# Revit family: C_BTCALU200_3D_CAD_MULT_Prod
name_source: partatom
category: Structural Connections
revit_build: Autodesk Revit 2015 (Build: 20140606_1530(x64)
units: mm (PartAtom-declared; Revit-internal decimal feet)

## types (1)
- C_BTCALU200_3D_CAD_MULT_Prod
    Default Elevation = 0 mm  [stored 0 ft]
    Density = 0.61 kg
    Description = Concealed beam hanger
    EPD = https://www.strongtie.eu
    ETA / DoP = https://www.strongtie.eu
    H = 200 mm  [stored 0.656168 ft]
    Manufacturer = Simpson Strong-Tie
    Model = BTCALU200
    Model Disclaimer = Contact Simpson Strong-Tie Company  for more information
    Model ID = 0080881108095439461087438277445270966215
    Name = BTCALU200
    ObjectType = BTCALU200
    Product Material = Aluminium
    Product Type = Concealed beam hanger
    Reference = BTCALU200
    SDD113 = SDD7.5x113
    SDD133 = SDD7.5x133
    SDD153 = SDD7.5x153
    SDD173 = SDD7.5x173
    SDD93 = SDD7.5x93
    STD10_100 = STD10X100
    STD10_120 = STD10X120
    STD10_140 = STD10X140
    STD10_160 = STD10X160
    STD10_60 = STD10X60
    STD10_80 = STD10X80
    STD12_100 = STD12X100
    STD12_120 = STD12X120
    STD12_140 = STD12X140
    STD12_160 = STD12X160
    STD12_60 = STD12X60
    STD12_80 = STD12X80
    STD8_100 = STD8X100
    STD8_120 = STD8X120
    STD8_140 = STD8X140
    STD8_160 = STD8X160
    STD8_60 = STD8X60
    STD8_80 = STD8X80
    Technical datasheet = https://www.strongtie.eu
    URL = www.strongtie.eu
    UniClass Number = Pr_20_29_31_13
    UniClass Title = Carbon steel punched metal plate fasteners
    W = 80 mm  [stored 0.262467 ft]

note: [stored X ft] marks values corroborated as IEEE doubles in the binary element streams (Revit-internal decimal feet)

## geometry (parser evidence)
native form markers: Blend x111, Sweep x43
no freeform markers — native parametric forms only
